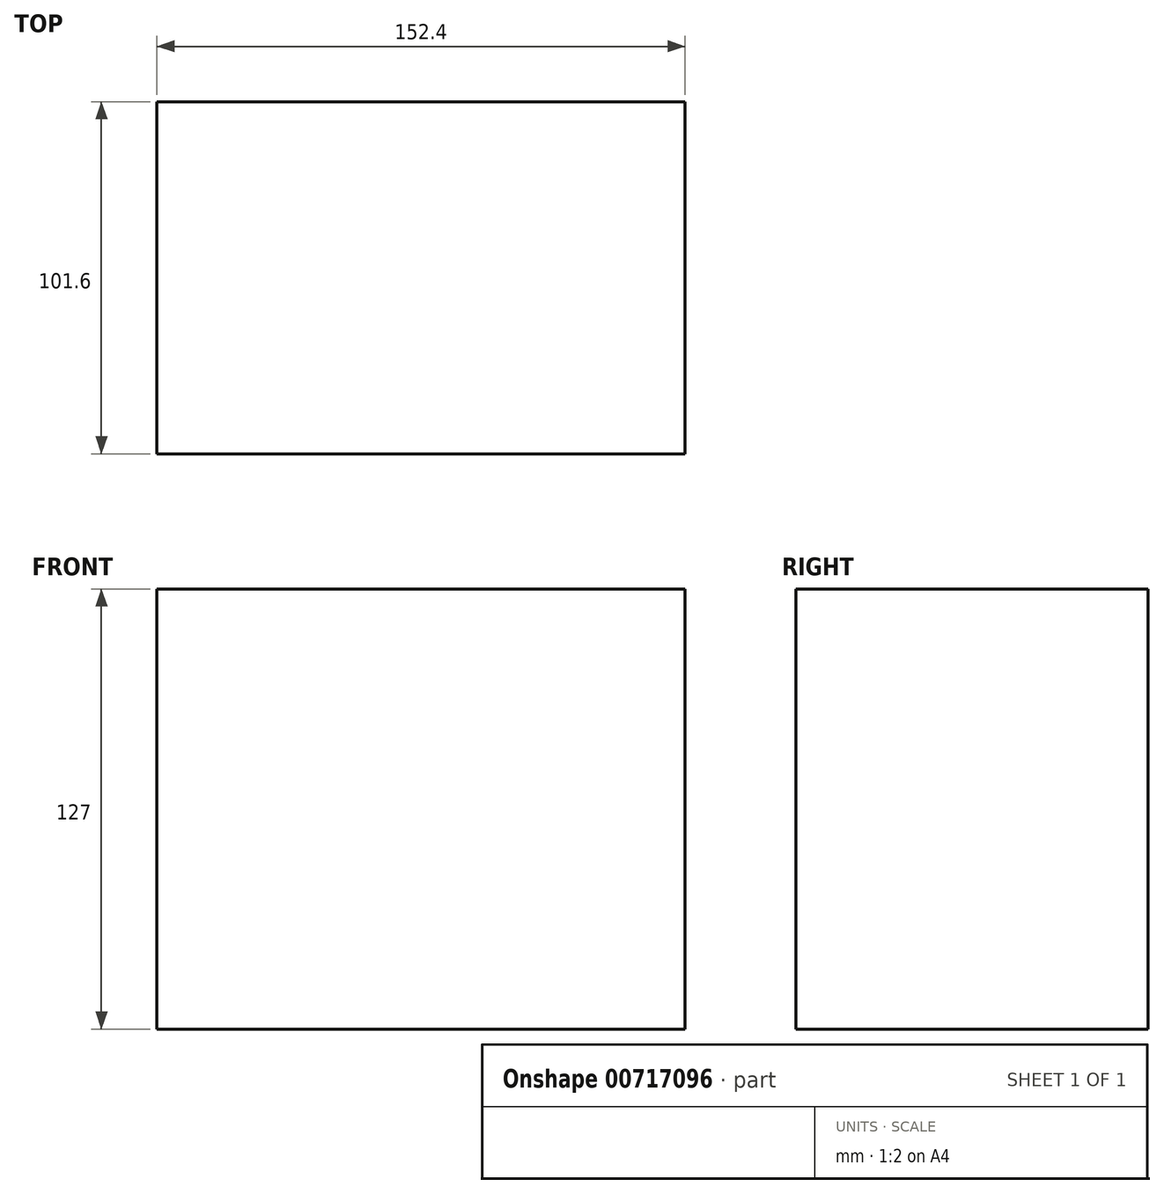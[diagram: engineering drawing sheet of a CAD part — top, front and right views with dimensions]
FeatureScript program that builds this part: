
annotation { "Feature Type Name" : "Feature", "Feature Type Description" : "" }
export const myFeature = defineFeature(function(context is Context, id is Id, definition is map)
    precondition{}
    {
        {
            var Q0;
            Q0=qCreatedBy(makeId("Front.planeOp"),FACE);
            var sketch = newSketch(context, id + "F0", { "sketchPlane" : qUnion([Q0])});
            skLineSegment(sketch, "E0", {"start": v(-99.14, 0) * mm, "end": v(53.26, 0) * mm});
            skLineSegment(sketch, "E1", {"start": v(53.26, 0) * mm, "end": v(53.26, 127) * mm});
            skLineSegment(sketch, "E2", {"start": v(53.26, 127) * mm, "end": v(-99.14, 127) * mm});
            skLineSegment(sketch, "E3", {"start": v(-99.14, 127) * mm, "end": v(-99.14, 0) * mm});
            skSolve(sketch);
        }
        {
            var Q0;
            Q0=makeQuery(id+"F0.imprint","IMPRINT",FACE,{"disambiguationData":[TD([[makeQuery(id+"F0.imprint","IMPRINT",EDGE,{"derivedFrom":sQuery(id+"F0.wireOp",EDGE,"E0")}),1.0]])]});
            extrude(context, id + "F1", {"entities" : qUnion([Q0]), "depth" : 101.6 * mm, "offsetDistance" : 25.4 * mm});
        }
    });
